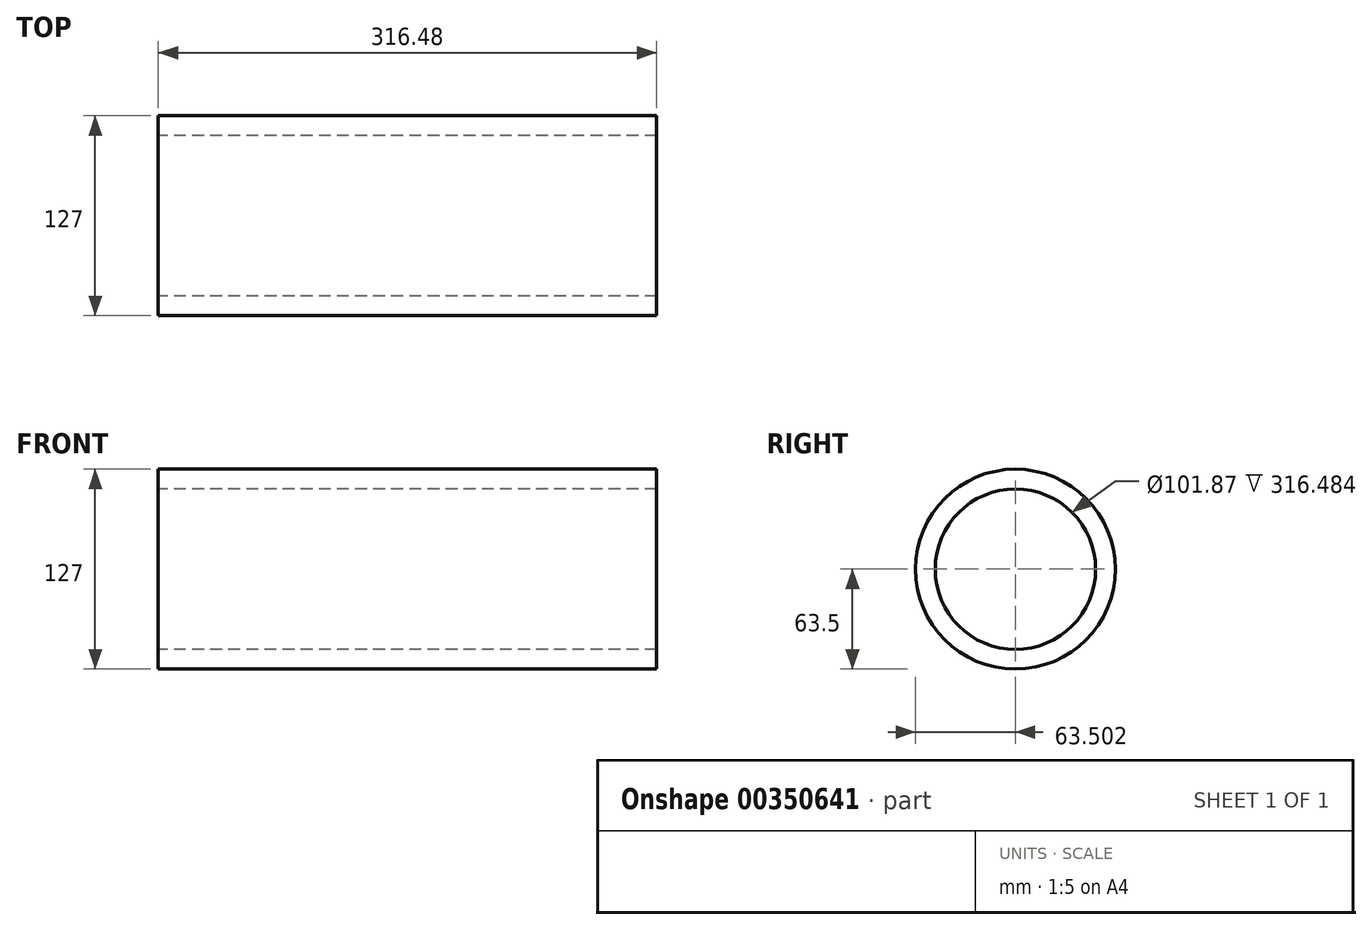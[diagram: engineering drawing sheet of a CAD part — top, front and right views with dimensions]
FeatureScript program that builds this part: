
annotation { "Feature Type Name" : "Feature", "Feature Type Description" : "" }
export const myFeature = defineFeature(function(context is Context, id is Id, definition is map)
    precondition{}
    {
        {
            var Q0;
            Q0=qCreatedBy(makeId("Front.planeOp"),FACE);
            var sketch = newSketch(context, id + "F0", { "sketchPlane" : qUnion([Q0])});
            skCircle(sketch, "E0", {"center": v(0, 0) * mm, "radius": 50.8 * mm});
            skCircle(sketch, "E1.0", {"center": v(0, 0) * mm, "radius": 39.62 * mm});
            skSolve(sketch);
        }
        {
            var Q0;
            Q0=qSketchRegion(id+"F0",true);
            extrude(context, id + "F1", {"entities" : qUnion([Q0]), "depth" : 189.23 * mm});
        }
        {
            var Q0;
            Q0=qCreatedBy(makeId("Right.planeOp"),FACE);
            var sketch = newSketch(context, id + "F2", { "sketchPlane" : qUnion([Q0])});
            skCircle(sketch, "E2", {"center": v(35.57, 0) * mm, "radius": 63.5 * mm});
            skCircle(sketch, "E3.0", {"center": v(35.57, 0) * mm, "radius": 50.94 * mm});
            skSolve(sketch);
        }
        {
            var Q0;
            Q0=makeQuery(id+"F2.imprint","IMPRINT",FACE,{"disambiguationData":[TD([[makeQuery(id+"F2.imprint","IMPRINT",EDGE,{"derivedFrom":sQuery(id+"F2.wireOp",EDGE,"E2")}),1.0]])]});
            extrude(context, id + "F3", {"entities" : qUnion([Q0]), "depth" : 316.48 * mm, "symmetric" : true});
        }
        {
            var Q0;
            Q0=makeQuery(id+"F3.opExtrude","SWEPT_BODY",BODY,{"disambiguationData":[OSD([sQuery(id+"F2.wireOp",EDGE,"E2"),sQuery(id+"F2.wireOp",EDGE,"E3.0")])]});
            var Q1;
            Q1=makeQuery(id+"F1.opExtrude","SWEPT_BODY",BODY,{"disambiguationData":[OSD([sQuery(id+"F0.wireOp",EDGE,"E0"),sQuery(id+"F0.wireOp",EDGE,"E1.0")])]});
            booleanBodies(context, id + "F4", {"operationType" : BooleanOperationType.SUBTRACTION, "tools" : qUnion([Q0]), "targets" : qUnion([Q1]), "keepTools" : true});
        }
        {
            var Q0;
            Q0=makeQuery(id+"F4.opBoolean","SPLIT",BODY,{"disambiguationData":[OD(1.0)],"derivedFrom":makeQuery(id+"F1.opExtrude","SWEPT_BODY",BODY,{"disambiguationData":[OSD([sQuery(id+"F0.wireOp",EDGE,"E0"),sQuery(id+"F0.wireOp",EDGE,"E1.0")])]})});
            var Q1;
            Q1=makeQuery(id+"F4.opBoolean","SPLIT",BODY,{"disambiguationData":[OD(2.0)],"derivedFrom":makeQuery(id+"F1.opExtrude","SWEPT_BODY",BODY,{"disambiguationData":[OSD([sQuery(id+"F0.wireOp",EDGE,"E0"),sQuery(id+"F0.wireOp",EDGE,"E1.0")])]})});
            deleteBodies(context, id + "F5", {"entities" : qUnion([Q0, Q1])});
        }
    });
